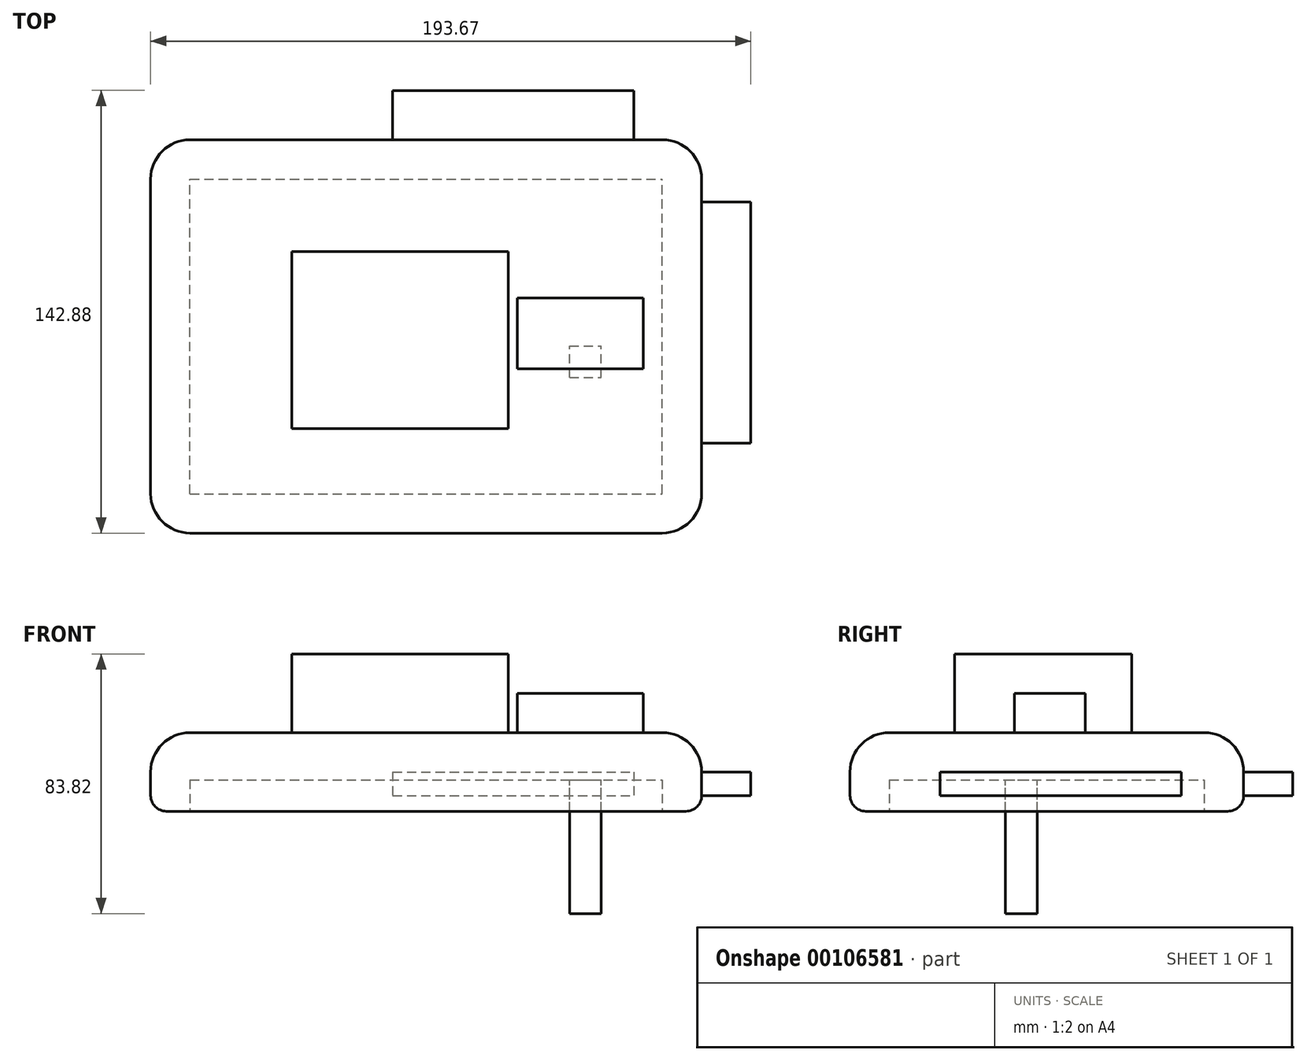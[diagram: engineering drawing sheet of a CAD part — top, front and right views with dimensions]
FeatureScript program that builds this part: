
annotation { "Feature Type Name" : "Feature", "Feature Type Description" : "" }
export const myFeature = defineFeature(function(context is Context, id is Id, definition is map)
    precondition{}
    {
        {
            var Q0;
            Q0=qCreatedBy(makeId("Front.planeOp"),FACE);
            var sketch = newSketch(context, id + "F0", { "sketchPlane" : qUnion([Q0])});
            skLineSegment(sketch, "E0.bottom", {"start": v(-82.55, 20.84) * mm, "end": v(95.25, 20.84) * mm});
            skLineSegment(sketch, "E0.top", {"start": v(-82.55, -4.56) * mm, "end": v(95.25, -4.56) * mm});
            skLineSegment(sketch, "E0.left", {"start": v(-82.55, 20.84) * mm, "end": v(-82.55, -4.56) * mm});
            skLineSegment(sketch, "E0.right", {"start": v(95.25, 20.84) * mm, "end": v(95.25, -4.56) * mm});
            skSolve(sketch);
        }
        {
            var Q0;
            Q0 = qSketchRegion(id + "F0", true);
            var Q1;
            Q1=makeQuery(id+"F0.imprint","IMPRINT",FACE,{"disambiguationData":[TD([[makeQuery(id+"F0.imprint","IMPRINT",EDGE,{"derivedFrom":sQuery(id+"F0.wireOp",EDGE,"E0.bottom")}),-1.0]])]});
            extrude(context, id + "F1", {"entities" : qUnion([Q0, Q1]), "depth" : 127 * mm});
        }
        {
            var Q0;
            Q0=makeQuery(id+"F1.opExtrude","CAP_EDGE",EDGE,{"disambiguationData":[OSD([sQuery(id+"F0.wireOp",EDGE,"E0.bottom")])],"isStart":false});
            var Q1;
            Q1=makeQuery(id+"F1.opExtrude","CAP_EDGE",EDGE,{"disambiguationData":[OSD([sQuery(id+"F0.wireOp",EDGE,"E0.left")])],"isStart":false});
            var Q2;
            Q2=makeQuery(id+"F1.opExtrude","SWEPT_EDGE",EDGE,{"disambiguationData":[OSD([sQuery(id+"F0.wireOp",EDGE,"E0.bottom"),sQuery(id+"F0.wireOp",EDGE,"E0.left")])]});
            fillet(context, id + "F2", {"entities" : qUnion([Q0, Q1, Q2]), "radius" : 12.7 * mm, "tangentPropagation" : true, "allowEdgeOverflow" : false});
        }
        {
            var Q0;
            Q0=makeQuery(id+"F1.opExtrude","SWEPT_EDGE",EDGE,{"disambiguationData":[OSD([sQuery(id+"F0.wireOp",EDGE,"E0.bottom"),sQuery(id+"F0.wireOp",EDGE,"E0.right")])]});
            var Q1;
            {var subQ0=sQuery(id+"F0.wireOp",EDGE,"E0.bottom");Q1=makeQuery(id+"F2.opFillet","BLEND_EDGE",EDGE,{"blendedFrom":[makeQuery(id+"F1.opExtrude","CAP_EDGE",EDGE,{"disambiguationData":[OSD([subQ0])],"isStart":false}),makeQuery(id+"F1.opExtrude","SWEPT_FACE",FACE,{"disambiguationData":[OSD([subQ0])]})],"blendedInto":[makeQuery(id+"F1.opExtrude","SWEPT_FACE",FACE,{"disambiguationData":[OSD([subQ0])]})]});}
            var Q2;
            Q2=makeQuery(id+"F1.opExtrude","CAP_EDGE",EDGE,{"disambiguationData":[OSD([sQuery(id+"F0.wireOp",EDGE,"E0.right")])],"isStart":false});
            fillet(context, id + "F3", {"entities" : qUnion([Q0, Q1, Q2]), "radius" : 12.7 * mm, "tangentPropagation" : true, "allowEdgeOverflow" : false});
        }
        {
            var Q0;
            Q0=makeQuery(id+"F1.opExtrude","CAP_EDGE",EDGE,{"disambiguationData":[OSD([sQuery(id+"F0.wireOp",EDGE,"E0.bottom")])],"isStart":true});
            var Q1;
            {var subQ0=sQuery(id+"F0.wireOp",EDGE,"E0.bottom");Q1=makeQuery(id+"F2.opFillet","BLEND_EDGE",EDGE,{"blendedFrom":[makeQuery(id+"F1.opExtrude","SWEPT_EDGE",EDGE,{"disambiguationData":[OSD([subQ0,sQuery(id+"F0.wireOp",EDGE,"E0.left")])]}),makeQuery(id+"F1.opExtrude","SWEPT_FACE",FACE,{"disambiguationData":[OSD([subQ0])]})],"blendedInto":[makeQuery(id+"F1.opExtrude","SWEPT_FACE",FACE,{"disambiguationData":[OSD([subQ0])]})]});}
            var Q2;
            Q2=makeQuery(id+"F1.opExtrude","CAP_EDGE",EDGE,{"disambiguationData":[OSD([sQuery(id+"F0.wireOp",EDGE,"E0.left")])],"isStart":true});
            fillet(context, id + "F4", {"entities" : qUnion([Q0, Q1, Q2]), "radius" : 12.7 * mm, "tangentPropagation" : true, "allowEdgeOverflow" : false});
        }
        {
            var Q0;
            Q0=makeQuery(id+"F1.opExtrude","SWEPT_FACE",FACE,{"disambiguationData":[OSD([sQuery(id+"F0.wireOp",EDGE,"E0.top")])]});
            var sketch = newSketch(context, id + "F5", { "sketchPlane" : qUnion([Q0])});
            skLineSegment(sketch, "E1.bottom", {"start": v(-69.85, 114.3) * mm, "end": v(82.55, 114.3) * mm});
            skLineSegment(sketch, "E1.top", {"start": v(-69.85, 12.7) * mm, "end": v(82.55, 12.7) * mm});
            skLineSegment(sketch, "E1.left", {"start": v(-69.85, 114.3) * mm, "end": v(-69.85, 12.7) * mm});
            skLineSegment(sketch, "E1.right", {"start": v(82.55, 114.3) * mm, "end": v(82.55, 12.7) * mm});
            skSolve(sketch);
        }
        {
            var Q0;
            Q0=makeQuery(id+"F5.imprint","IMPRINT",FACE,{"disambiguationData":[TD([[makeQuery(id+"F5.imprint","IMPRINT",EDGE,{"derivedFrom":sQuery(id+"F5.wireOp",EDGE,"E1.bottom")}),-1.0]])]});
            extrude(context, id + "F6", {"entities" : qUnion([Q0]), "operationType" : NewBodyOperationType.REMOVE, "oppositeDirection" : true, "depth" : 10.16 * mm});
        }
        {
            var Q0;
            Q0=makeQuery(id+"F1.opExtrude","CAP_EDGE",EDGE,{"disambiguationData":[OSD([sQuery(id+"F0.wireOp",EDGE,"E0.top")])],"isStart":false});
            var Q1;
            Q1=makeQuery(id+"F1.opExtrude","SWEPT_EDGE",EDGE,{"disambiguationData":[OSD([sQuery(id+"F0.wireOp",EDGE,"E0.top"),sQuery(id+"F0.wireOp",EDGE,"E0.right")])]});
            var Q2;
            Q2=makeQuery(id+"F3.opFillet","BLEND_EDGE",EDGE,{"blendedFrom":[makeQuery(id+"F1.opExtrude","CAP_EDGE",EDGE,{"disambiguationData":[OSD([sQuery(id+"F0.wireOp",EDGE,"E0.right")])],"isStart":false}),makeQuery(id+"F1.opExtrude","SWEPT_FACE",FACE,{"disambiguationData":[OSD([sQuery(id+"F0.wireOp",EDGE,"E0.top")])]})],"blendedInto":[makeQuery(id+"F1.opExtrude","SWEPT_FACE",FACE,{"disambiguationData":[OSD([sQuery(id+"F0.wireOp",EDGE,"E0.top")])]})]});
            fillet(context, id + "F7", {"entities" : qUnion([Q0, Q1, Q2]), "radius" : 5.08 * mm, "tangentPropagation" : true, "allowEdgeOverflow" : false});
        }
        {
            var Q0;
            Q0=makeQuery(id+"F6.boolean.opBoolean","COPY",FACE,{"derivedFrom":makeQuery(id+"F6.opExtrude","CAP_FACE",FACE,{"disambiguationData":[OSD([sQuery(id+"F5.wireOp",EDGE,"E1.bottom"),sQuery(id+"F5.wireOp",EDGE,"E1.top"),sQuery(id+"F5.wireOp",EDGE,"E1.left"),sQuery(id+"F5.wireOp",EDGE,"E1.right")])],"isStart":false})});
            var sketch = newSketch(context, id + "F8", { "sketchPlane" : qUnion([Q0])});
            skLineSegment(sketch, "E2.bottom", {"start": v(52.58, 76.82) * mm, "end": v(62.74, 76.82) * mm});
            skLineSegment(sketch, "E2.top", {"start": v(52.58, 66.66) * mm, "end": v(62.74, 66.66) * mm});
            skLineSegment(sketch, "E2.left", {"start": v(52.58, 76.82) * mm, "end": v(52.58, 66.66) * mm});
            skLineSegment(sketch, "E2.right", {"start": v(62.74, 76.82) * mm, "end": v(62.74, 66.66) * mm});
            skSolve(sketch);
        }
        {
            var Q0;
            Q0=makeQuery(id+"F8.imprint","IMPRINT",FACE,{"disambiguationData":[TD([[makeQuery(id+"F8.imprint","IMPRINT",EDGE,{"derivedFrom":sQuery(id+"F8.wireOp",EDGE,"E2.bottom")}),-1.0]])]});
            extrude(context, id + "F9", {"entities" : qUnion([Q0]), "operationType" : NewBodyOperationType.ADD, "depth" : 43.18 * mm});
        }
        {
            var Q0;
            Q0=makeQuery(id+"F1.opExtrude","SWEPT_FACE",FACE,{"disambiguationData":[OSD([sQuery(id+"F0.wireOp",EDGE,"E0.bottom")])]});
            var sketch = newSketch(context, id + "F10", { "sketchPlane" : qUnion([Q0])});
            skLineSegment(sketch, "E3.bottom", {"start": v(-37.04, -36.15) * mm, "end": v(32.8, -36.15) * mm});
            skLineSegment(sketch, "E3.top", {"start": v(-37.04, -93.3) * mm, "end": v(32.8, -93.3) * mm});
            skLineSegment(sketch, "E3.left", {"start": v(-37.04, -36.15) * mm, "end": v(-37.04, -93.3) * mm});
            skLineSegment(sketch, "E3.right", {"start": v(32.8, -36.15) * mm, "end": v(32.8, -93.3) * mm});
            skLineSegment(sketch, "E4.bottom", {"start": v(35.77, -51.1) * mm, "end": v(76.41, -51.1) * mm});
            skLineSegment(sketch, "E4.top", {"start": v(35.77, -73.96) * mm, "end": v(76.41, -73.96) * mm});
            skLineSegment(sketch, "E4.left", {"start": v(35.77, -51.1) * mm, "end": v(35.77, -73.96) * mm});
            skLineSegment(sketch, "E4.right", {"start": v(76.41, -51.1) * mm, "end": v(76.41, -73.96) * mm});
            skSolve(sketch);
        }
        {
            var Q0;
            Q0=makeQuery(id+"F10.imprint","IMPRINT",FACE,{"disambiguationData":[TD([[makeQuery(id+"F10.imprint","IMPRINT",EDGE,{"derivedFrom":sQuery(id+"F10.wireOp",EDGE,"E3.bottom")}),-1.0]])]});
            extrude(context, id + "F11", {"entities" : qUnion([Q0]), "operationType" : NewBodyOperationType.ADD, "depth" : 25.4 * mm});
        }
        {
            var Q0;
            Q0=makeQuery(id+"F10.imprint","IMPRINT",FACE,{"disambiguationData":[TD([[makeQuery(id+"F10.imprint","IMPRINT",EDGE,{"derivedFrom":sQuery(id+"F10.wireOp",EDGE,"E4.bottom")}),-1.0]])]});
            extrude(context, id + "F12", {"entities" : qUnion([Q0]), "operationType" : NewBodyOperationType.ADD, "depth" : 12.7 * mm});
        }
        {
            var Q0;
            Q0=makeQuery(id+"F1.opExtrude","SWEPT_FACE",FACE,{"disambiguationData":[OSD([sQuery(id+"F0.wireOp",EDGE,"E0.right")])]});
            var sketch = newSketch(context, id + "F13", { "sketchPlane" : qUnion([Q0])});
            skLineSegment(sketch, "E5.bottom", {"start": v(-97.95, 8.46) * mm, "end": v(-20.16, 8.46) * mm});
            skLineSegment(sketch, "E5.top", {"start": v(-97.95, 0.52) * mm, "end": v(-20.16, 0.52) * mm});
            skLineSegment(sketch, "E5.left", {"start": v(-97.95, 8.46) * mm, "end": v(-97.95, 0.52) * mm});
            skLineSegment(sketch, "E5.right", {"start": v(-20.16, 8.46) * mm, "end": v(-20.16, 0.52) * mm});
            skSolve(sketch);
        }
        {
            var Q0;
            {var subQ0=sQuery(id+"F13.wireOp",EDGE,"E5.top");Q0=makeQuery(id+"F13.imprint","IMPRINT",FACE,{"disambiguationData":[TD([[makeQuery(id+"F13.imprint","IMPRINT",EDGE,{"derivedFrom":subQ0}),1.0]])]});}
            extrude(context, id + "F14", {"entities" : qUnion([Q0]), "operationType" : NewBodyOperationType.ADD, "depth" : 15.88 * mm});
        }
        {
            var Q0;
            Q0=makeQuery(id+"F1.opExtrude","CAP_FACE",FACE,{"disambiguationData":[OSD([sQuery(id+"F0.wireOp",EDGE,"E0.bottom"),sQuery(id+"F0.wireOp",EDGE,"E0.top"),sQuery(id+"F0.wireOp",EDGE,"E0.left"),sQuery(id+"F0.wireOp",EDGE,"E0.right")])],"isStart":true});
            var sketch = newSketch(context, id + "F15", { "sketchPlane" : qUnion([Q0])});
            skLineSegment(sketch, "E6.bottom", {"start": v(-73.32, 8.14) * mm, "end": v(4.46, 8.14) * mm});
            skLineSegment(sketch, "E6.top", {"start": v(-73.32, 0.52) * mm, "end": v(4.46, 0.52) * mm});
            skLineSegment(sketch, "E6.left", {"start": v(-73.32, 8.14) * mm, "end": v(-73.32, 0.52) * mm});
            skLineSegment(sketch, "E6.right", {"start": v(4.46, 8.14) * mm, "end": v(4.46, 0.52) * mm});
            skSolve(sketch);
        }
        {
            var Q0;
            Q0=makeQuery(id+"F15.imprint","IMPRINT",FACE,{"disambiguationData":[TD([[makeQuery(id+"F15.imprint","IMPRINT",EDGE,{"derivedFrom":sQuery(id+"F15.wireOp",EDGE,"E6.bottom")}),1.0]])]});
            extrude(context, id + "F16", {"entities" : qUnion([Q0]), "operationType" : NewBodyOperationType.ADD, "depth" : 15.88 * mm});
        }
    });
